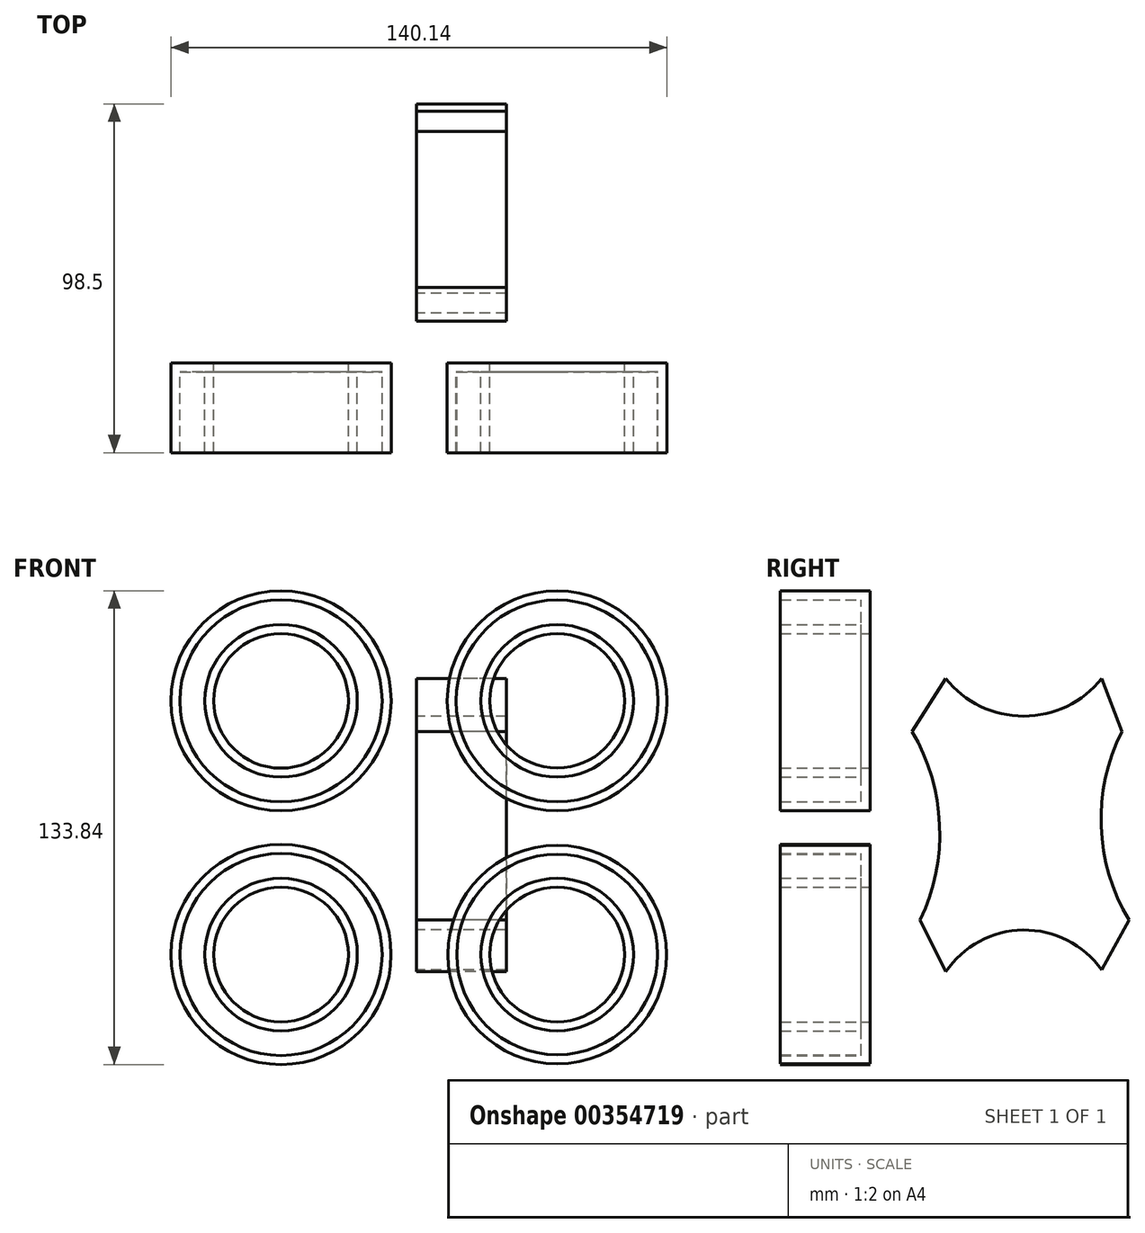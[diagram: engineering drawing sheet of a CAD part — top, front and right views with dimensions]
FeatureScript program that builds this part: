
annotation { "Feature Type Name" : "Feature", "Feature Type Description" : "" }
export const myFeature = defineFeature(function(context is Context, id is Id, definition is map)
    precondition{}
    {
        {
            var Q0;
            Q0=qCreatedBy(makeId("Front.planeOp"),FACE);
            var sketch = newSketch(context, id + "F0", { "sketchPlane" : qUnion([Q0])});
            skCircle(sketch, "E0", {"center": v(-38.28, 37.41) * mm, "radius": 31.1 * mm});
            skCircle(sketch, "E1", {"center": v(39.72, 37.41) * mm, "radius": 31.06 * mm});
            skCircle(sketch, "E2", {"center": v(39.72, -34.25) * mm, "radius": 30.88 * mm});
            skCircle(sketch, "E3", {"center": v(-38.28, -34.25) * mm, "radius": 31.08 * mm});
            skCircle(sketch, "E4", {"center": v(-38.28, 37.41) * mm, "radius": 19.01 * mm});
            skCircle(sketch, "E5", {"center": v(39.72, 37.41) * mm, "radius": 19 * mm});
            skCircle(sketch, "E6", {"center": v(39.72, -34.25) * mm, "radius": 19.01 * mm});
            skCircle(sketch, "E7", {"center": v(-38.28, -34.25) * mm, "radius": 19.01 * mm});
            skSolve(sketch);
        }
        {
            var Q0;
            Q0 = qSketchRegion(id + "F0", true);
            extrude(context, id + "F1", {"entities" : qUnion([Q0]), "depth" : 25.4 * mm});
        }
        {
            var Q0;
            Q0=makeQuery(id+"F1.opExtrude","CAP_FACE",FACE,{"disambiguationData":[OSD([sQuery(id+"F0.wireOp",EDGE,"E0"),sQuery(id+"F0.wireOp",EDGE,"E4")])],"isStart":false});
            var Q1;
            Q1=makeQuery(id+"F1.opExtrude","CAP_FACE",FACE,{"disambiguationData":[OSD([sQuery(id+"F0.wireOp",EDGE,"E1"),sQuery(id+"F0.wireOp",EDGE,"E5")])],"isStart":false});
            var Q2;
            Q2=makeQuery(id+"F1.opExtrude","CAP_FACE",FACE,{"disambiguationData":[OSD([sQuery(id+"F0.wireOp",EDGE,"E2"),sQuery(id+"F0.wireOp",EDGE,"E6")])],"isStart":false});
            var Q3;
            Q3=makeQuery(id+"F1.opExtrude","CAP_FACE",FACE,{"disambiguationData":[OSD([sQuery(id+"F0.wireOp",EDGE,"E3"),sQuery(id+"F0.wireOp",EDGE,"E7")])],"isStart":false});
            shell(context, id + "F2", {"entities" : qUnion([Q0, Q1, Q2, Q3]), "thickness" : 2.54 * mm});
        }
        {
            var Q0;
            Q0=qCreatedBy(makeId("Right.planeOp"),FACE);
            var sketch = newSketch(context, id + "F3", { "sketchPlane" : qUnion([Q0])});
            skArc(sketch, "E8", {"start": v(21.3, 43.75) * mm, "mid": v(43.31, 33.1) * mm, "end": v(65.33, 43.75) * mm});
            skArc(sketch, "E9", {"start": v(65.33, -38.57) * mm, "mid": v(43.16, -27.32) * mm, "end": v(21.3, -39.14) * mm});
            skArc(sketch, "E10", {"start": v(14.1, -24.46) * mm, "mid": v(19.56, 2.44) * mm, "end": v(11.8, 28.78) * mm});
            skArc(sketch, "E11", {"start": v(71.09, 28.78) * mm, "mid": v(65.2, 1.9) * mm, "end": v(73.1, -24.46) * mm});
            skLineSegment(sketch, "E12", {"start": v(14.1, -24.46) * mm, "end": v(21.3, -39.14) * mm});
            skLineSegment(sketch, "E13", {"start": v(65.33, -38.57) * mm, "end": v(73.1, -24.46) * mm});
            skLineSegment(sketch, "E14", {"start": v(71.09, 28.78) * mm, "end": v(65.33, 43.75) * mm});
            skLineSegment(sketch, "E15", {"start": v(11.8, 28.78) * mm, "end": v(21.3, 43.75) * mm});
            skSolve(sketch);
        }
        {
            var Q0;
            Q0 = qSketchRegion(id + "F3", true);
            extrude(context, id + "F4", {"entities" : qUnion([Q0]), "depth" : 25.4 * mm});
        }
    });
